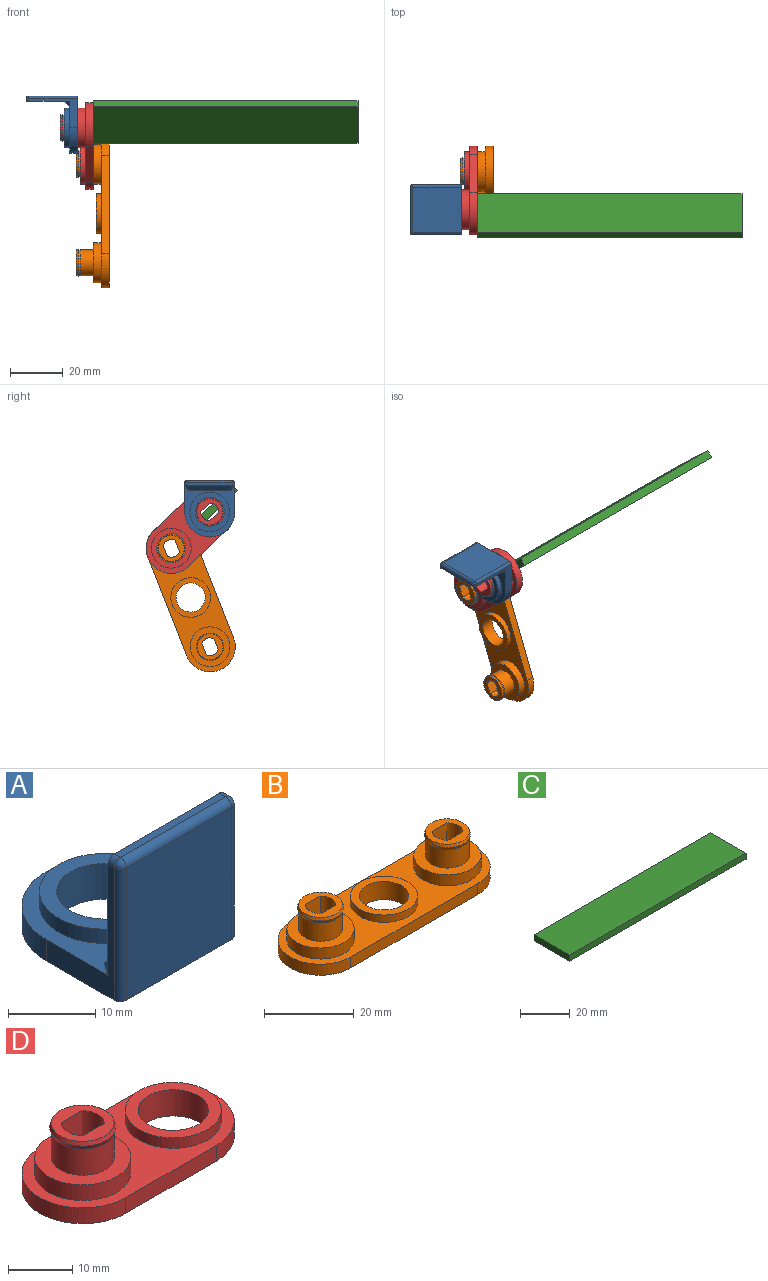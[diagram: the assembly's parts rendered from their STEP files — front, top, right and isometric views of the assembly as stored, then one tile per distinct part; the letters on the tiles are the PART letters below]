
ASSEMBLY  parts=4 mates=3
PART A: 21 faces, bbox 19x21.5x19.5 mm
  f0: plane 18.5x11mm, normal (1,0,0), area 48.5mm2, adj f1,f5,f6,f9,f13,f15,f17
  f1: cylinder r=9.5mm len=19mm, axis (0,0,-1), area 89.5mm2, adj f0,f2,f5,f6
  f2: plane 18.5x11mm, normal (-1,0,0), area 48.5mm2, adj f1,f5,f6,f9,f12,f14,f16
  f3: plane 18.5x17mm, normal (0,-1,0), area 314.5mm2, adj f6,f16,f17,f20
  f4: cylinder r=5.5mm len=11mm, axis (0,0,-1), area 172.8mm2, adj f6,f8
  f5: plane 19.49x19mm, normal (0,0,1), area 119.9mm2, adj f0,f1,f2,f7,f11,f14,f15
  f6: plane 21.5x19mm, normal (0,0,-1), area 274.3mm2, adj f0,f1,f2,f3,f4,f16,f17
  f7: cylinder r=7.5mm len=15mm, axis (0,0,-1), area 94.2mm2, adj f5,f8
  f8: plane 15x15mm, normal (0,0,1), area 81.7mm2, adj f4,f7
  f9: plane 19x16.49mm, normal (0,1,0), area 277.9mm2, adj f0,f2,f10,f11,f12,f13,f14,f15
  f10: plane 17x1mm, normal (0,0,1), area 17mm2, adj f9,f12,f13,f20
  f11: plane 16.18x2mm, normal (0,0.71,0.71), area 45.8mm2, adj f5,f9,f14,f15
  f12: cylinder r=1mm len=1mm, axis (0,1,0), area 1.6mm2, adj f2,f9,f10,f18
  f13: cylinder r=1mm len=1mm, axis (0,-1,0), area 1.6mm2, adj f0,f9,f10,f19
  f14: plane 2x2mm, normal (-0.71,0.5,0.5), area 2.8mm2, adj f2,f5,f9,f11
  f15: plane 2x2mm, normal (0.71,0.5,0.5), area 2.8mm2, adj f0,f5,f9,f11
  f16: cylinder r=1mm len=18.5mm, axis (0,0,-1), area 29.1mm2, adj f2,f3,f6,f18
  f17: cylinder r=1mm len=18.5mm, axis (0,0,-1), area 29.1mm2, adj f0,f3,f6,f19
  f18: sphere r=1mm, area 1.6mm2, adj f12,f16,f20
  f19: sphere r=1mm, area 1.6mm2, adj f13,f17,f20
  f20: cylinder r=1mm len=17mm, axis (-1,0,0), area 26.7mm2, adj f3,f10,f18,f19
PART B: 29 faces, bbox 59x19x12.5 mm
  f0: cylinder r=9.5mm len=19mm, axis (0,0,-1), area 89.5mm2, adj f1,f4,f5,f6
  f1: plane 40x3mm, normal (0,-1,0), area 120mm2, adj f0,f2,f5,f6
  f2: cylinder r=9.5mm len=19mm, axis (0,0,-1), area 89.5mm2, adj f1,f4,f5,f6
  f3: cylinder r=5.5mm len=11mm, axis (0,0,-1), area 172.8mm2, adj f6,f9
  f4: plane 40x3mm, normal (0,1,0), area 120mm2, adj f0,f2,f5,f6
  f5: plane 59x19mm, normal (0,0,1), area 513.4mm2, adj f0,f1,f2,f4,f7,f8,f10
  f6: plane 59x19mm, normal (0,0,-1), area 889.3mm2, adj f0,f1,f2,f3,f4,f11,f12,f13
  f7: cylinder r=7.5mm len=15mm, axis (0,0,-1), area 141.4mm2, adj f5,f15
  f8: cylinder r=7.5mm len=15mm, axis (0,0,-1), area 94.2mm2, adj f5,f9
  f9: plane 15x15mm, normal (0,0,1), area 81.7mm2, adj f3,f8
  f10: cylinder r=7.5mm len=15mm, axis (0,0,-1), area 141.4mm2, adj f5,f24
  f11: cylinder r=3.35mm len=12.5mm, axis (0,0,-1), area 68.7mm2, adj f6,f12,f14,f17
  f12: plane 12.5x4.57mm, normal (0,1,0), area 57.1mm2, adj f6,f11,f13,f17
  f13: cylinder r=3.35mm len=12.5mm, axis (0,0,-1), area 68.7mm2, adj f6,f12,f14,f17
  f14: plane 12.5x4.57mm, normal (0,-1,0), area 57.1mm2, adj f6,f11,f13,f17
  f15: plane 15x15mm, normal (0,0,1), area 101.3mm2, adj f7,f16
  f16: cylinder r=4.9mm len=9.8mm, axis (0,0,-1), area 153.9mm2, adj f15,f18
  f17: plane 9.8x9.8mm, normal (0,0,1), area 45.8mm2, adj f11,f12,f13,f14,f19
  f18: cone r=5.15mm half-angle=18.4deg, axis (0,0,1), area 25mm2, adj f16,f19
  f19: cone r=4.9mm half-angle=18.4deg, axis (0,0,-1), area 25mm2, adj f17,f18
  f20: cylinder r=3.35mm len=12.5mm, axis (0,0,-1), area 68.7mm2, adj f6,f21,f23,f26
  f21: plane 12.5x4.57mm, normal (0,1,0), area 57.1mm2, adj f6,f20,f22,f26
  f22: cylinder r=3.35mm len=12.5mm, axis (0,0,-1), area 68.7mm2, adj f6,f21,f23,f26
  f23: plane 12.5x4.57mm, normal (0,-1,0), area 57.1mm2, adj f6,f20,f22,f26
  f24: plane 15x15mm, normal (0,0,1), area 101.3mm2, adj f10,f25
  f25: cylinder r=4.9mm len=9.8mm, axis (0,0,-1), area 153.9mm2, adj f24,f27
  f26: plane 9.8x9.8mm, normal (0,0,1), area 45.8mm2, adj f20,f21,f22,f23,f28
  f27: cone r=5.15mm half-angle=18.4deg, axis (0,0,1), area 25mm2, adj f25,f28
  f28: cone r=4.9mm half-angle=18.4deg, axis (0,0,-1), area 25mm2, adj f26,f27
PART C: 6 faces, bbox 100x20x3 mm
  f0: plane 100x3mm, normal (0,1,0), area 300mm2, adj f1,f3,f4,f5
  f1: plane 20x3mm, normal (-1,0,0), area 60mm2, adj f0,f2,f4,f5
  f2: plane 100x3mm, normal (0,-1,0), area 300mm2, adj f1,f3,f4,f5
  f3: plane 20x3mm, normal (1,0,0), area 60mm2, adj f0,f2,f4,f5
  f4: plane 100x20mm, normal (0,0,1), area 2000mm2, adj f0,f1,f2,f3
  f5: plane 100x20mm, normal (0,0,-1), area 2000mm2, adj f0,f1,f2,f3
PART D: 19 faces, bbox 39x19x12.5 mm
  f0: cylinder r=9.5mm len=19mm, axis (0,0,-1), area 89.5mm2, adj f1,f3,f5,f6
  f1: plane 20x3mm, normal (0,-1,0), area 60mm2, adj f0,f2,f5,f6
  f2: cylinder r=9.5mm len=19mm, axis (0,0,-1), area 89.5mm2, adj f1,f3,f5,f6
  f3: plane 20x3mm, normal (0,1,0), area 60mm2, adj f0,f2,f5,f6
  f4: cylinder r=5.5mm len=11mm, axis (0,0,-1), area 172.8mm2, adj f6,f9
  f5: plane 39x19mm, normal (0,0,1), area 310.1mm2, adj f0,f1,f2,f3,f7,f8
  f6: plane 39x19mm, normal (0,0,-1), area 538.9mm2, adj f0,f1,f2,f3,f4,f10,f11,f12
  f7: cylinder r=7.5mm len=15mm, axis (0,0,-1), area 141.4mm2, adj f5,f14
  f8: cylinder r=7.5mm len=15mm, axis (0,0,-1), area 94.2mm2, adj f5,f9
  f9: plane 15x15mm, normal (0,0,1), area 81.7mm2, adj f4,f8
  f10: cylinder r=3.35mm len=12.5mm, axis (0,0,-1), area 68.7mm2, adj f6,f11,f13,f16
  f11: plane 12.5x4.57mm, normal (0,1,0), area 57.1mm2, adj f6,f10,f12,f16
  f12: cylinder r=3.35mm len=12.5mm, axis (0,0,-1), area 68.7mm2, adj f6,f11,f13,f16
  f13: plane 12.5x4.57mm, normal (0,-1,0), area 57.1mm2, adj f6,f10,f12,f16
  f14: plane 15x15mm, normal (0,0,1), area 101.3mm2, adj f7,f15
  f15: cylinder r=4.9mm len=9.8mm, axis (0,0,-1), area 153.9mm2, adj f14,f17
  f16: plane 9.8x9.8mm, normal (0,0,1), area 45.8mm2, adj f10,f11,f12,f13,f18
  f17: cone r=5.15mm half-angle=18.4deg, axis (0,0,1), area 25mm2, adj f15,f18
  f18: cone r=4.9mm half-angle=18.4deg, axis (0,0,-1), area 25mm2, adj f16,f17
PLACE A rot(axis=(-0.58,-0.58,0.58),120deg) t=(29.25,0,83)mm
PLACE B rot(axis=(0.7,-0.13,-0.7),164.8deg) t=(41.25,14.52,69.24)mm
PLACE C rot(axis=(-1,0,0),43.5deg) t=(35.25,-10.62,91)mm
PLACE D rot(axis=(-0.68,-0.29,0.68),147.6deg) t=(35.25,0,83)mm
MATE fastened D.f6 <-> C.f1  axis (1,0,0) through (35.25,6.38,76.96)mm
MATE revolute A.f1 <-> D.f0  axis (-1,0,0) through (24.25,0,83)mm
MATE revolute B.f0 <-> D.f2  axis (1,0,0) through (30.25,14.52,69.24)mm
